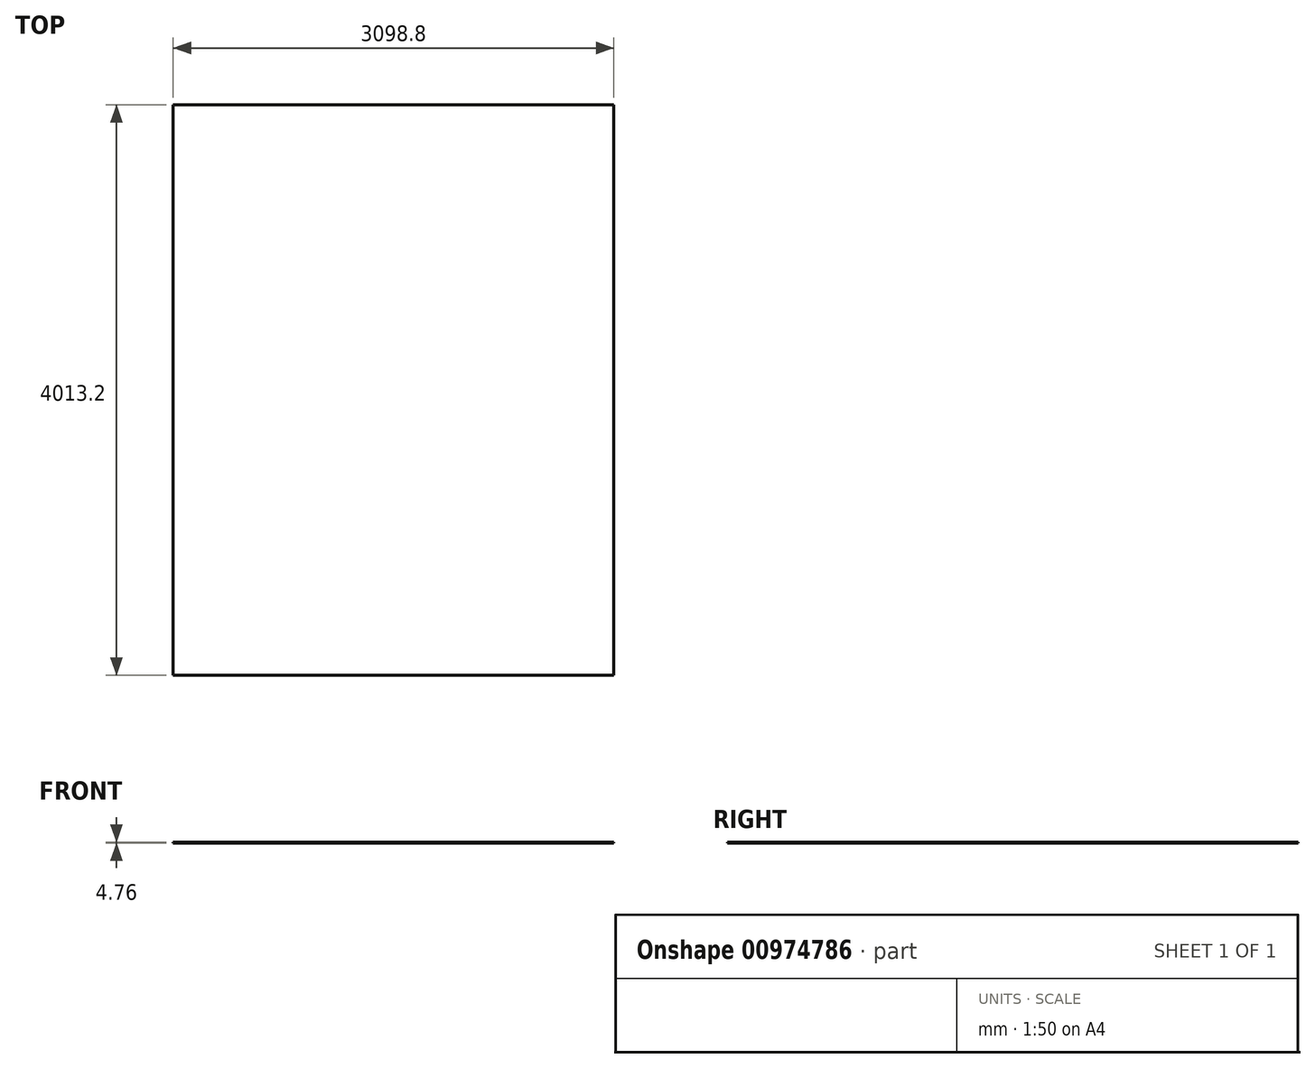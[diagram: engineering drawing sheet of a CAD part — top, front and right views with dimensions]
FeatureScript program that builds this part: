
annotation { "Feature Type Name" : "Feature", "Feature Type Description" : "" }
export const myFeature = defineFeature(function(context is Context, id is Id, definition is map)
    precondition{}
    {
        {
            var Q0;
            Q0=qCreatedBy(makeId("Top.planeOp"),FACE);
            var sketch = newSketch(context, id + "F0", { "sketchPlane" : qUnion([Q0])});
            skLineSegment(sketch, "E0.bottom", {"start": v(1549.4, -2006.6) * mm, "end": v(-1549.4, -2006.6) * mm});
            skLineSegment(sketch, "E0.top", {"start": v(1549.4, 2006.6) * mm, "end": v(-1549.4, 2006.6) * mm});
            skLineSegment(sketch, "E0.left", {"start": v(1549.4, -2006.6) * mm, "end": v(1549.4, 2006.6) * mm});
            skLineSegment(sketch, "E0.right", {"start": v(-1549.4, -2006.6) * mm, "end": v(-1549.4, 2006.6) * mm});
            skPoint(sketch, "E0.middle", {"position": v(0, 0) * mm});
            skSolve(sketch);
        }
        {
            var Q0;
            Q0=makeQuery(id+"F0.imprint","IMPRINT",FACE,{"disambiguationData":[TD([[makeQuery(id+"F0.imprint","IMPRINT",EDGE,{"derivedFrom":sQuery(id+"F0.wireOp",EDGE,"E0.bottom")}),-1.0]])]});
            extrude(context, id + "F1", {"entities" : qUnion([Q0]), "depth" : 4.76 * mm, "offsetDistance" : 25.4 * mm});
        }
    });
